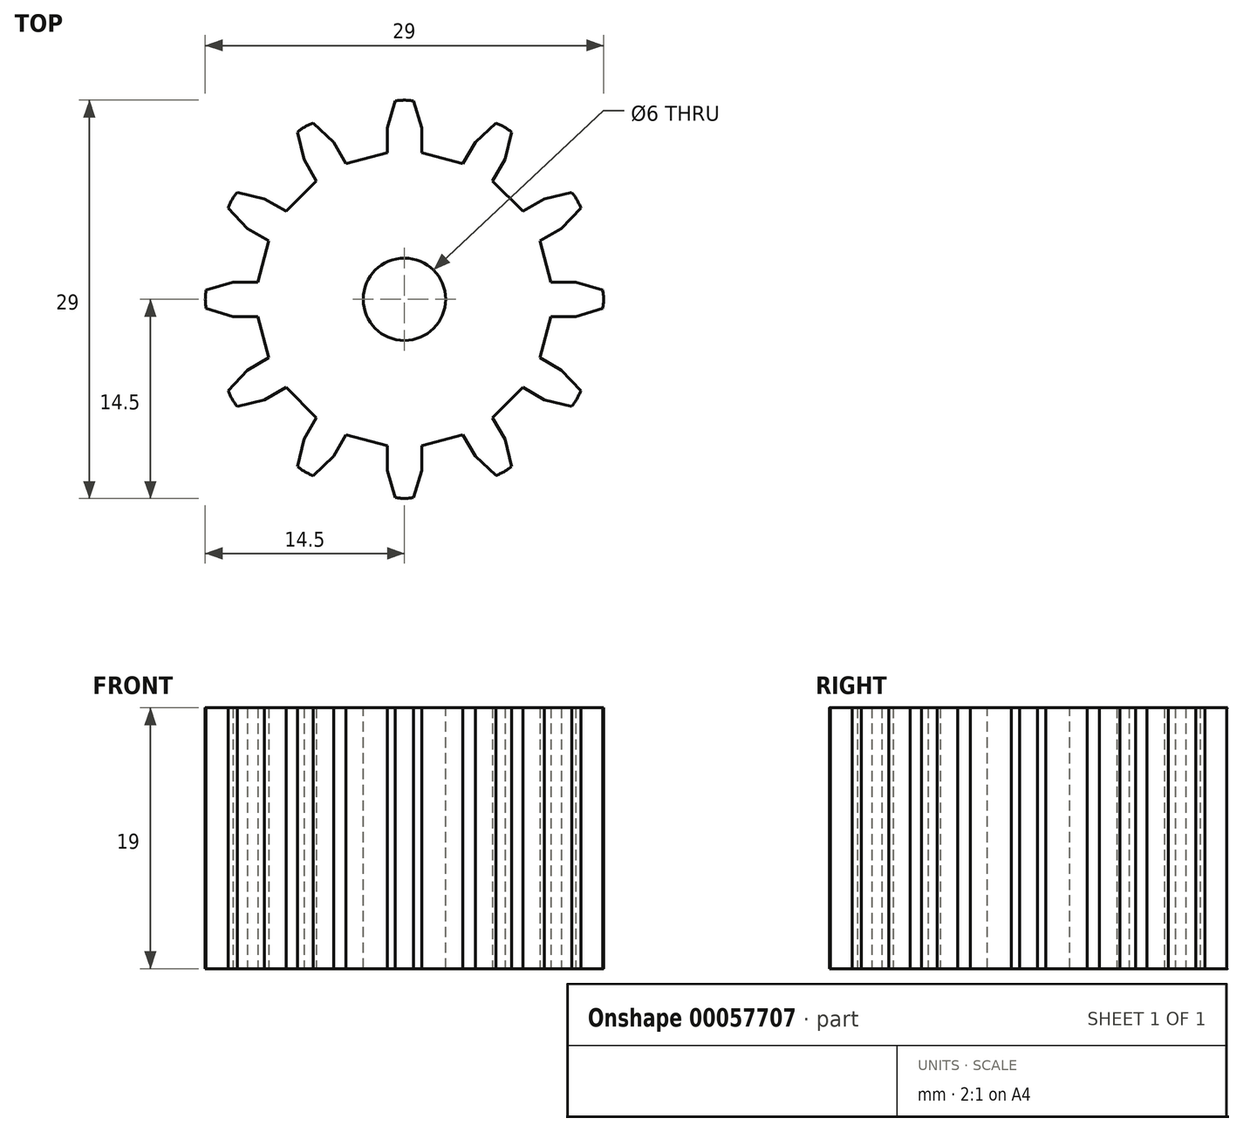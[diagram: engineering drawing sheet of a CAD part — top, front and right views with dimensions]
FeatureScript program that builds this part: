
annotation { "Feature Type Name" : "Feature", "Feature Type Description" : "" }
export const myFeature = defineFeature(function(context is Context, id is Id, definition is map)
    precondition{}
    {
        {
            var Q0;
            Q0=qCreatedBy(makeId("Top.planeOp"),FACE);
            var sketch = newSketch(context, id + "F0", { "sketchPlane" : qUnion([Q0])});
            skCircle(sketch, "E0", {"center": v(0, 0) * mm, "radius": 14.5 * mm});
            skArc(sketch, "E1", {"start": v(-1.25, 10.68) * mm, "mid": v(0, -10.75) * mm, "end": v(1.25, 10.68) * mm});
            skLineSegment(sketch, "E2", {"start": v(0, 10.75) * mm, "end": v(0, 14.5) * mm});
            skLineSegment(sketch, "E3.0", {"start": v(1.25, 10.68) * mm, "end": v(1.25, 14.29) * mm});
            skLineSegment(sketch, "E4.0", {"start": v(-1.25, 10.68) * mm, "end": v(-1.25, 14.29) * mm});
            skArc(sketch, "E5.trimOffspring", {"start": v(1.25, 14.29) * mm, "mid": v(0, 14.5) * mm, "end": v(-1.25, 14.29) * mm});
            skLineSegment(sketch, "E6", {"start": v(-1.25, 14.29) * mm, "end": v(-1.25, 14.45) * mm});
            skLineSegment(sketch, "E7.1.0", {"start": v(-4.26, 9.87) * mm, "end": v(-6.06, 13) * mm});
            skArc(sketch, "E7.1.1", {"start": v(-6.06, 13) * mm, "mid": v(-7.25, 12.56) * mm, "end": v(-8.23, 11.75) * mm});
            skLineSegment(sketch, "E7.1.2", {"start": v(-6.42, 8.62) * mm, "end": v(-8.23, 11.75) * mm});
            skLineSegment(sketch, "E7.2.0", {"start": v(-8.62, 6.42) * mm, "end": v(-11.75, 8.23) * mm});
            skArc(sketch, "E7.2.1", {"start": v(-11.75, 8.23) * mm, "mid": v(-12.56, 7.25) * mm, "end": v(-13, 6.06) * mm});
            skLineSegment(sketch, "E7.2.2", {"start": v(-9.87, 4.26) * mm, "end": v(-13, 6.06) * mm});
            skLineSegment(sketch, "E7.3.0", {"start": v(-10.68, 1.25) * mm, "end": v(-14.29, 1.25) * mm});
            skArc(sketch, "E7.3.1", {"start": v(-14.29, 1.25) * mm, "mid": v(-14.5, 0) * mm, "end": v(-14.29, -1.25) * mm});
            skLineSegment(sketch, "E7.3.2", {"start": v(-10.68, -1.25) * mm, "end": v(-14.29, -1.25) * mm});
            skLineSegment(sketch, "E7.4.0", {"start": v(-9.87, -4.26) * mm, "end": v(-13, -6.06) * mm});
            skArc(sketch, "E7.4.1", {"start": v(-13, -6.06) * mm, "mid": v(-12.56, -7.25) * mm, "end": v(-11.75, -8.23) * mm});
            skLineSegment(sketch, "E7.4.2", {"start": v(-8.62, -6.42) * mm, "end": v(-11.75, -8.23) * mm});
            skLineSegment(sketch, "E7.5.0", {"start": v(-6.42, -8.62) * mm, "end": v(-8.23, -11.75) * mm});
            skArc(sketch, "E7.5.1", {"start": v(-8.23, -11.75) * mm, "mid": v(-7.25, -12.56) * mm, "end": v(-6.06, -13) * mm});
            skLineSegment(sketch, "E7.5.2", {"start": v(-4.26, -9.87) * mm, "end": v(-6.06, -13) * mm});
            skLineSegment(sketch, "E7.6.0", {"start": v(-1.25, -10.68) * mm, "end": v(-1.25, -14.29) * mm});
            skArc(sketch, "E7.6.1", {"start": v(-1.25, -14.29) * mm, "mid": v(0, -14.5) * mm, "end": v(1.25, -14.29) * mm});
            skLineSegment(sketch, "E7.6.2", {"start": v(1.25, -10.68) * mm, "end": v(1.25, -14.29) * mm});
            skLineSegment(sketch, "E7.7.0", {"start": v(4.26, -9.87) * mm, "end": v(6.06, -13) * mm});
            skArc(sketch, "E7.7.1", {"start": v(6.06, -13) * mm, "mid": v(7.25, -12.56) * mm, "end": v(8.23, -11.75) * mm});
            skLineSegment(sketch, "E7.7.2", {"start": v(6.42, -8.62) * mm, "end": v(8.23, -11.75) * mm});
            skLineSegment(sketch, "E7.8.0", {"start": v(8.62, -6.42) * mm, "end": v(11.75, -8.23) * mm});
            skArc(sketch, "E7.8.1", {"start": v(11.75, -8.23) * mm, "mid": v(12.56, -7.25) * mm, "end": v(13, -6.06) * mm});
            skLineSegment(sketch, "E7.8.2", {"start": v(9.87, -4.26) * mm, "end": v(13, -6.06) * mm});
            skLineSegment(sketch, "E7.9.0", {"start": v(10.68, -1.25) * mm, "end": v(14.29, -1.25) * mm});
            skArc(sketch, "E7.9.1", {"start": v(14.29, -1.25) * mm, "mid": v(14.5, 0) * mm, "end": v(14.29, 1.25) * mm});
            skLineSegment(sketch, "E7.9.2", {"start": v(10.68, 1.25) * mm, "end": v(14.29, 1.25) * mm});
            skLineSegment(sketch, "E7.10.0", {"start": v(9.87, 4.26) * mm, "end": v(13, 6.06) * mm});
            skArc(sketch, "E7.10.1", {"start": v(13, 6.06) * mm, "mid": v(12.56, 7.25) * mm, "end": v(11.75, 8.23) * mm});
            skLineSegment(sketch, "E7.10.2", {"start": v(8.62, 6.42) * mm, "end": v(11.75, 8.23) * mm});
            skLineSegment(sketch, "E7.11.0", {"start": v(6.42, 8.62) * mm, "end": v(8.23, 11.75) * mm});
            skArc(sketch, "E7.11.1", {"start": v(8.23, 11.75) * mm, "mid": v(7.25, 12.56) * mm, "end": v(6.06, 13) * mm});
            skLineSegment(sketch, "E7.11.2", {"start": v(4.26, 9.87) * mm, "end": v(6.06, 13) * mm});
            skLineSegment(sketch, "E8", {"start": v(-1.25, 14.45) * mm, "end": v(-0.66, 14.45) * mm});
            skLineSegment(sketch, "E9", {"start": v(-0.66, 14.45) * mm, "end": v(-1.25, 12.48) * mm});
            skLineSegment(sketch, "E10.MirrorCS", {"start": v(0.66, 14.45) * mm, "end": v(1.25, 12.48) * mm});
            skLineSegment(sketch, "E11.1.0", {"start": v(-7.8, 12.18) * mm, "end": v(-7.32, 10.18) * mm});
            skLineSegment(sketch, "E11.1.1", {"start": v(-6.65, 12.84) * mm, "end": v(-5.16, 11.43) * mm});
            skLineSegment(sketch, "E11.2.0", {"start": v(-12.84, 6.65) * mm, "end": v(-11.43, 5.16) * mm});
            skLineSegment(sketch, "E11.2.1", {"start": v(-12.18, 7.8) * mm, "end": v(-10.18, 7.32) * mm});
            skLineSegment(sketch, "E11.3.0", {"start": v(-14.45, -0.66) * mm, "end": v(-12.48, -1.25) * mm});
            skLineSegment(sketch, "E11.3.1", {"start": v(-14.45, 0.66) * mm, "end": v(-12.48, 1.25) * mm});
            skLineSegment(sketch, "E11.4.0", {"start": v(-12.18, -7.8) * mm, "end": v(-10.18, -7.32) * mm});
            skLineSegment(sketch, "E11.4.1", {"start": v(-12.84, -6.65) * mm, "end": v(-11.43, -5.16) * mm});
            skLineSegment(sketch, "E11.5.0", {"start": v(-6.65, -12.84) * mm, "end": v(-5.16, -11.43) * mm});
            skLineSegment(sketch, "E11.5.1", {"start": v(-7.8, -12.18) * mm, "end": v(-7.32, -10.18) * mm});
            skLineSegment(sketch, "E11.6.0", {"start": v(0.66, -14.45) * mm, "end": v(1.25, -12.48) * mm});
            skLineSegment(sketch, "E11.6.1", {"start": v(-0.66, -14.45) * mm, "end": v(-1.25, -12.48) * mm});
            skLineSegment(sketch, "E11.7.0", {"start": v(7.8, -12.18) * mm, "end": v(7.32, -10.18) * mm});
            skLineSegment(sketch, "E11.7.1", {"start": v(6.65, -12.84) * mm, "end": v(5.16, -11.43) * mm});
            skLineSegment(sketch, "E11.8.0", {"start": v(12.84, -6.65) * mm, "end": v(11.43, -5.16) * mm});
            skLineSegment(sketch, "E11.8.1", {"start": v(12.18, -7.8) * mm, "end": v(10.18, -7.32) * mm});
            skLineSegment(sketch, "E11.9.0", {"start": v(14.45, 0.66) * mm, "end": v(12.48, 1.25) * mm});
            skLineSegment(sketch, "E11.9.1", {"start": v(14.45, -0.66) * mm, "end": v(12.48, -1.25) * mm});
            skLineSegment(sketch, "E11.10.0", {"start": v(12.18, 7.8) * mm, "end": v(10.18, 7.32) * mm});
            skLineSegment(sketch, "E11.10.1", {"start": v(12.84, 6.65) * mm, "end": v(11.43, 5.16) * mm});
            skLineSegment(sketch, "E11.11.0", {"start": v(6.65, 12.84) * mm, "end": v(5.16, 11.43) * mm});
            skLineSegment(sketch, "E11.11.1", {"start": v(7.8, 12.18) * mm, "end": v(7.32, 10.18) * mm});
            skSolve(sketch);
        }
        {
            var Q0;
            {var subQ0=sQuery(id+"F0.wireOp",EDGE,"E1");var subQ22=sQuery(id+"F0.wireOp",EDGE,"E4.0");var subQ23=makeQuery(id+"F0.imprint","INTERSECT",VERTEX,{"derivedFrom":[subQ0,subQ22]});Q0=makeQuery(id+"F0.imprint","IMPRINT",FACE,{"disambiguationData":[TD([[makeQuery(id+"F0.imprint","IMPRINT",EDGE,{"disambiguationData":[TD([[subQ23,-1.0]])],"derivedFrom":subQ0}),1.0]])]});}
            var Q1;
            {var subQ6=sQuery(id+"F0.wireOp",EDGE,"E7.1.0");var subQ7=sQuery(id+"F0.wireOp",EDGE,"E1");var subQ8=makeQuery(id+"F0.imprint","INTERSECT",VERTEX,{"derivedFrom":[subQ7,subQ6]});Q1=makeQuery(id+"F0.imprint","IMPRINT",FACE,{"disambiguationData":[TD([[makeQuery(id+"F0.imprint","IMPRINT",EDGE,{"disambiguationData":[TD([[subQ8,-1.0]])],"derivedFrom":subQ7}),-1.0]])]});}
            var Q2;
            {var subQ6=sQuery(id+"F0.wireOp",EDGE,"E7.2.0");var subQ7=sQuery(id+"F0.wireOp",EDGE,"E1");var subQ8=makeQuery(id+"F0.imprint","INTERSECT",VERTEX,{"derivedFrom":[subQ7,subQ6]});Q2=makeQuery(id+"F0.imprint","IMPRINT",FACE,{"disambiguationData":[TD([[makeQuery(id+"F0.imprint","IMPRINT",EDGE,{"disambiguationData":[TD([[subQ8,-1.0]])],"derivedFrom":subQ7}),-1.0]])]});}
            var Q3;
            {var subQ8=sQuery(id+"F0.wireOp",EDGE,"E7.3.0");var subQ9=sQuery(id+"F0.wireOp",EDGE,"E1");var subQ10=makeQuery(id+"F0.imprint","INTERSECT",VERTEX,{"derivedFrom":[subQ9,subQ8]});Q3=makeQuery(id+"F0.imprint","IMPRINT",FACE,{"disambiguationData":[TD([[makeQuery(id+"F0.imprint","IMPRINT",EDGE,{"disambiguationData":[TD([[subQ10,-1.0]])],"derivedFrom":subQ9}),-1.0]])]});}
            var Q4;
            {var subQ6=sQuery(id+"F0.wireOp",EDGE,"E7.11.0");var subQ7=sQuery(id+"F0.wireOp",EDGE,"E1");var subQ8=makeQuery(id+"F0.imprint","INTERSECT",VERTEX,{"derivedFrom":[subQ7,subQ6]});Q4=makeQuery(id+"F0.imprint","IMPRINT",FACE,{"disambiguationData":[TD([[makeQuery(id+"F0.imprint","IMPRINT",EDGE,{"disambiguationData":[TD([[subQ8,-1.0]])],"derivedFrom":subQ7}),-1.0]])]});}
            var Q5;
            {var subQ4=sQuery(id+"F0.wireOp",EDGE,"E7.10.0");var subQ5=sQuery(id+"F0.wireOp",EDGE,"E1");var subQ6=makeQuery(id+"F0.imprint","INTERSECT",VERTEX,{"derivedFrom":[subQ5,subQ4]});Q5=makeQuery(id+"F0.imprint","IMPRINT",FACE,{"disambiguationData":[TD([[makeQuery(id+"F0.imprint","IMPRINT",EDGE,{"disambiguationData":[TD([[subQ6,-1.0]])],"derivedFrom":subQ5}),-1.0]])]});}
            var Q6;
            {var subQ6=sQuery(id+"F0.wireOp",EDGE,"E7.9.0");var subQ7=sQuery(id+"F0.wireOp",EDGE,"E1");var subQ8=makeQuery(id+"F0.imprint","INTERSECT",VERTEX,{"derivedFrom":[subQ7,subQ6]});Q6=makeQuery(id+"F0.imprint","IMPRINT",FACE,{"disambiguationData":[TD([[makeQuery(id+"F0.imprint","IMPRINT",EDGE,{"disambiguationData":[TD([[subQ8,-1.0]])],"derivedFrom":subQ7}),-1.0]])]});}
            var Q7;
            {var subQ6=sQuery(id+"F0.wireOp",EDGE,"E7.6.0");var subQ7=sQuery(id+"F0.wireOp",EDGE,"E1");var subQ8=makeQuery(id+"F0.imprint","INTERSECT",VERTEX,{"derivedFrom":[subQ7,subQ6]});Q7=makeQuery(id+"F0.imprint","IMPRINT",FACE,{"disambiguationData":[TD([[makeQuery(id+"F0.imprint","IMPRINT",EDGE,{"disambiguationData":[TD([[subQ8,-1.0]])],"derivedFrom":subQ7}),-1.0]])]});}
            var Q8;
            {var subQ0=sQuery(id+"F0.wireOp",EDGE,"E7.5.0");var subQ1=sQuery(id+"F0.wireOp",EDGE,"E1");var subQ2=makeQuery(id+"F0.imprint","INTERSECT",VERTEX,{"derivedFrom":[subQ1,subQ0]});Q8=makeQuery(id+"F0.imprint","IMPRINT",FACE,{"disambiguationData":[TD([[makeQuery(id+"F0.imprint","IMPRINT",EDGE,{"disambiguationData":[TD([[subQ2,-1.0]])],"derivedFrom":subQ1}),-1.0]])]});}
            var Q9;
            {var subQ6=sQuery(id+"F0.wireOp",EDGE,"E7.4.0");var subQ7=sQuery(id+"F0.wireOp",EDGE,"E1");var subQ8=makeQuery(id+"F0.imprint","INTERSECT",VERTEX,{"derivedFrom":[subQ7,subQ6]});Q9=makeQuery(id+"F0.imprint","IMPRINT",FACE,{"disambiguationData":[TD([[makeQuery(id+"F0.imprint","IMPRINT",EDGE,{"disambiguationData":[TD([[subQ8,-1.0]])],"derivedFrom":subQ7}),-1.0]])]});}
            var Q10;
            {var subQ4=sQuery(id+"F0.wireOp",EDGE,"E7.8.0");var subQ5=sQuery(id+"F0.wireOp",EDGE,"E1");var subQ6=makeQuery(id+"F0.imprint","INTERSECT",VERTEX,{"derivedFrom":[subQ5,subQ4]});Q10=makeQuery(id+"F0.imprint","IMPRINT",FACE,{"disambiguationData":[TD([[makeQuery(id+"F0.imprint","IMPRINT",EDGE,{"disambiguationData":[TD([[subQ6,-1.0]])],"derivedFrom":subQ5}),-1.0]])]});}
            var Q11;
            {var subQ6=sQuery(id+"F0.wireOp",EDGE,"E7.7.0");var subQ7=sQuery(id+"F0.wireOp",EDGE,"E1");var subQ8=makeQuery(id+"F0.imprint","INTERSECT",VERTEX,{"derivedFrom":[subQ7,subQ6]});Q11=makeQuery(id+"F0.imprint","IMPRINT",FACE,{"disambiguationData":[TD([[makeQuery(id+"F0.imprint","IMPRINT",EDGE,{"disambiguationData":[TD([[subQ8,-1.0]])],"derivedFrom":subQ7}),-1.0]])]});}
            extrude(context, id + "F1", {"entities" : qUnion([Q0, Q1, Q2, Q3, Q4, Q5, Q6, Q7, Q8, Q9, Q10, Q11]), "depth" : 19 * mm});
        }
        {
            var Q0;
            Q0=makeQuery(id+"F1.opExtrude","CAP_FACE",FACE,{"disambiguationData":[OSD([sQuery(id+"F0.wireOp",EDGE,"E1"),sQuery(id+"F0.wireOp",EDGE,"E3.0"),sQuery(id+"F0.wireOp",EDGE,"E4.0"),sQuery(id+"F0.wireOp",EDGE,"E5.trimOffspring"),sQuery(id+"F0.wireOp",EDGE,"E7.1.0"),sQuery(id+"F0.wireOp",EDGE,"E7.1.1"),sQuery(id+"F0.wireOp",EDGE,"E7.1.2"),sQuery(id+"F0.wireOp",EDGE,"E7.2.0"),sQuery(id+"F0.wireOp",EDGE,"E7.2.1"),sQuery(id+"F0.wireOp",EDGE,"E7.2.2"),sQuery(id+"F0.wireOp",EDGE,"E7.3.0"),sQuery(id+"F0.wireOp",EDGE,"E7.3.1"),sQuery(id+"F0.wireOp",EDGE,"E7.3.2"),sQuery(id+"F0.wireOp",EDGE,"E7.4.0"),sQuery(id+"F0.wireOp",EDGE,"E7.4.1"),sQuery(id+"F0.wireOp",EDGE,"E7.4.2"),sQuery(id+"F0.wireOp",EDGE,"E7.5.0"),sQuery(id+"F0.wireOp",EDGE,"E7.5.1"),sQuery(id+"F0.wireOp",EDGE,"E7.5.2"),sQuery(id+"F0.wireOp",EDGE,"E7.6.0"),sQuery(id+"F0.wireOp",EDGE,"E7.6.1"),sQuery(id+"F0.wireOp",EDGE,"E7.6.2"),sQuery(id+"F0.wireOp",EDGE,"E7.7.0"),sQuery(id+"F0.wireOp",EDGE,"E7.7.1"),sQuery(id+"F0.wireOp",EDGE,"E7.7.2"),sQuery(id+"F0.wireOp",EDGE,"E7.8.0"),sQuery(id+"F0.wireOp",EDGE,"E7.8.1"),sQuery(id+"F0.wireOp",EDGE,"E7.8.2"),sQuery(id+"F0.wireOp",EDGE,"E7.9.0"),sQuery(id+"F0.wireOp",EDGE,"E7.9.1"),sQuery(id+"F0.wireOp",EDGE,"E7.9.2"),sQuery(id+"F0.wireOp",EDGE,"E7.10.0"),sQuery(id+"F0.wireOp",EDGE,"E7.10.1"),sQuery(id+"F0.wireOp",EDGE,"E7.10.2"),sQuery(id+"F0.wireOp",EDGE,"E7.11.0"),sQuery(id+"F0.wireOp",EDGE,"E7.11.1"),sQuery(id+"F0.wireOp",EDGE,"E7.11.2")])],"isStart":false});
            var sketch = newSketch(context, id + "F2", { "sketchPlane" : qUnion([Q0])});
            skCircle(sketch, "E12", {"center": v(0, 0) * mm, "radius": 3 * mm});
            skSolve(sketch);
        }
        {
            var Q0;
            Q0 = qSketchRegion(id + "F2", true);
            extrude(context, id + "F3", {"entities" : qUnion([Q0]), "operationType" : NewBodyOperationType.REMOVE, "endBound" : BoundingType.THROUGH_ALL, "oppositeDirection" : true, "depth" : 25 * mm});
        }
        {
            var Q0;
            Q0=makeQuery(id+"F1.opExtrude","CAP_FACE",FACE,{"disambiguationData":[OSD([sQuery(id+"F0.wireOp",EDGE,"E1"),sQuery(id+"F0.wireOp",EDGE,"E3.0"),sQuery(id+"F0.wireOp",EDGE,"E4.0"),sQuery(id+"F0.wireOp",EDGE,"E5.trimOffspring"),sQuery(id+"F0.wireOp",EDGE,"E7.1.0"),sQuery(id+"F0.wireOp",EDGE,"E7.1.1"),sQuery(id+"F0.wireOp",EDGE,"E7.1.2"),sQuery(id+"F0.wireOp",EDGE,"E7.2.0"),sQuery(id+"F0.wireOp",EDGE,"E7.2.1"),sQuery(id+"F0.wireOp",EDGE,"E7.2.2"),sQuery(id+"F0.wireOp",EDGE,"E7.3.0"),sQuery(id+"F0.wireOp",EDGE,"E7.3.1"),sQuery(id+"F0.wireOp",EDGE,"E7.3.2"),sQuery(id+"F0.wireOp",EDGE,"E7.4.0"),sQuery(id+"F0.wireOp",EDGE,"E7.4.1"),sQuery(id+"F0.wireOp",EDGE,"E7.4.2"),sQuery(id+"F0.wireOp",EDGE,"E7.5.0"),sQuery(id+"F0.wireOp",EDGE,"E7.5.1"),sQuery(id+"F0.wireOp",EDGE,"E7.5.2"),sQuery(id+"F0.wireOp",EDGE,"E7.6.0"),sQuery(id+"F0.wireOp",EDGE,"E7.6.1"),sQuery(id+"F0.wireOp",EDGE,"E7.6.2"),sQuery(id+"F0.wireOp",EDGE,"E7.7.0"),sQuery(id+"F0.wireOp",EDGE,"E7.7.1"),sQuery(id+"F0.wireOp",EDGE,"E7.7.2"),sQuery(id+"F0.wireOp",EDGE,"E7.8.0"),sQuery(id+"F0.wireOp",EDGE,"E7.8.1"),sQuery(id+"F0.wireOp",EDGE,"E7.8.2"),sQuery(id+"F0.wireOp",EDGE,"E7.9.0"),sQuery(id+"F0.wireOp",EDGE,"E7.9.1"),sQuery(id+"F0.wireOp",EDGE,"E7.9.2"),sQuery(id+"F0.wireOp",EDGE,"E7.10.0"),sQuery(id+"F0.wireOp",EDGE,"E7.10.1"),sQuery(id+"F0.wireOp",EDGE,"E7.10.2"),sQuery(id+"F0.wireOp",EDGE,"E7.11.0"),sQuery(id+"F0.wireOp",EDGE,"E7.11.1"),sQuery(id+"F0.wireOp",EDGE,"E7.11.2")])],"isStart":false});
            var sketch = newSketch(context, id + "F4", { "sketchPlane" : qUnion([Q0])});
            skLineSegment(sketch, "E13", {"start": v(1.25, 10.68) * mm, "end": v(4.26, 9.87) * mm});
            skLineSegment(sketch, "E14", {"start": v(4.26, 9.87) * mm, "end": v(6.42, 8.62) * mm});
            skLineSegment(sketch, "E15", {"start": v(6.42, 8.62) * mm, "end": v(8.62, 6.42) * mm});
            skLineSegment(sketch, "E16", {"start": v(8.62, 6.42) * mm, "end": v(9.87, 4.26) * mm});
            skLineSegment(sketch, "E17", {"start": v(9.87, 4.26) * mm, "end": v(10.68, 1.25) * mm});
            skLineSegment(sketch, "E18", {"start": v(10.68, 1.25) * mm, "end": v(10.68, -1.25) * mm});
            skLineSegment(sketch, "E19", {"start": v(10.68, -1.25) * mm, "end": v(9.87, -4.26) * mm});
            skLineSegment(sketch, "E20", {"start": v(9.87, -4.26) * mm, "end": v(8.62, -6.42) * mm});
            skLineSegment(sketch, "E21", {"start": v(8.62, -6.42) * mm, "end": v(6.42, -8.62) * mm});
            skLineSegment(sketch, "E22", {"start": v(6.42, -8.62) * mm, "end": v(4.26, -9.87) * mm});
            skLineSegment(sketch, "E23", {"start": v(4.26, -9.87) * mm, "end": v(1.25, -10.68) * mm});
            skLineSegment(sketch, "E24", {"start": v(1.25, -10.68) * mm, "end": v(-1.25, -10.68) * mm});
            skLineSegment(sketch, "E25", {"start": v(-1.25, -10.68) * mm, "end": v(-4.26, -9.87) * mm});
            skLineSegment(sketch, "E26", {"start": v(-4.26, -9.87) * mm, "end": v(-6.42, -8.62) * mm});
            skLineSegment(sketch, "E27", {"start": v(-6.42, -8.62) * mm, "end": v(-8.62, -6.42) * mm});
            skLineSegment(sketch, "E28", {"start": v(-8.62, -6.42) * mm, "end": v(-9.87, -4.26) * mm});
            skLineSegment(sketch, "E29", {"start": v(-9.87, -4.26) * mm, "end": v(-10.68, -1.25) * mm});
            skLineSegment(sketch, "E30", {"start": v(-10.68, -1.25) * mm, "end": v(-10.68, 1.25) * mm});
            skLineSegment(sketch, "E31", {"start": v(-10.68, 1.25) * mm, "end": v(-9.87, 4.26) * mm});
            skLineSegment(sketch, "E32", {"start": v(-9.87, 4.26) * mm, "end": v(-8.62, 6.42) * mm});
            skLineSegment(sketch, "E33", {"start": v(-8.62, 6.42) * mm, "end": v(-6.42, 8.62) * mm});
            skLineSegment(sketch, "E34", {"start": v(-6.42, 8.62) * mm, "end": v(-4.26, 9.87) * mm});
            skLineSegment(sketch, "E35", {"start": v(-4.26, 9.87) * mm, "end": v(-1.25, 10.68) * mm});
            skLineSegment(sketch, "E36", {"start": v(-1.25, 10.68) * mm, "end": v(1.25, 10.68) * mm});
            skSolve(sketch);
        }
        {
            var Q0;
            Q0=makeQuery(id+"F4.imprint","IMPRINT",FACE,{"disambiguationData":[TD([[makeQuery(id+"F4.imprint","IMPRINT",EDGE,{"derivedFrom":sQuery(id+"F4.wireOp",EDGE,"E31")}),1.0]])]});
            var Q1;
            Q1=makeQuery(id+"F4.imprint","IMPRINT",FACE,{"disambiguationData":[TD([[makeQuery(id+"F4.imprint","IMPRINT",EDGE,{"derivedFrom":sQuery(id+"F4.wireOp",EDGE,"E29")}),1.0]])]});
            var Q2;
            Q2=makeQuery(id+"F4.imprint","IMPRINT",FACE,{"disambiguationData":[TD([[makeQuery(id+"F4.imprint","IMPRINT",EDGE,{"derivedFrom":sQuery(id+"F4.wireOp",EDGE,"E33")}),1.0]])]});
            var Q3;
            Q3=makeQuery(id+"F4.imprint","IMPRINT",FACE,{"disambiguationData":[TD([[makeQuery(id+"F4.imprint","IMPRINT",EDGE,{"derivedFrom":sQuery(id+"F4.wireOp",EDGE,"E35")}),1.0]])]});
            var Q4;
            Q4=makeQuery(id+"F4.imprint","IMPRINT",FACE,{"disambiguationData":[TD([[makeQuery(id+"F4.imprint","IMPRINT",EDGE,{"derivedFrom":sQuery(id+"F4.wireOp",EDGE,"E13")}),1.0]])]});
            var Q5;
            Q5=makeQuery(id+"F4.imprint","IMPRINT",FACE,{"disambiguationData":[TD([[makeQuery(id+"F4.imprint","IMPRINT",EDGE,{"derivedFrom":sQuery(id+"F4.wireOp",EDGE,"E15")}),1.0]])]});
            var Q6;
            Q6=makeQuery(id+"F4.imprint","IMPRINT",FACE,{"disambiguationData":[TD([[makeQuery(id+"F4.imprint","IMPRINT",EDGE,{"derivedFrom":sQuery(id+"F4.wireOp",EDGE,"E17")}),1.0]])]});
            var Q7;
            Q7=makeQuery(id+"F4.imprint","IMPRINT",FACE,{"disambiguationData":[TD([[makeQuery(id+"F4.imprint","IMPRINT",EDGE,{"derivedFrom":sQuery(id+"F4.wireOp",EDGE,"E19")}),1.0]])]});
            var Q8;
            Q8=makeQuery(id+"F4.imprint","IMPRINT",FACE,{"disambiguationData":[TD([[makeQuery(id+"F4.imprint","IMPRINT",EDGE,{"derivedFrom":sQuery(id+"F4.wireOp",EDGE,"E21")}),1.0]])]});
            var Q9;
            Q9=makeQuery(id+"F4.imprint","IMPRINT",FACE,{"disambiguationData":[TD([[makeQuery(id+"F4.imprint","IMPRINT",EDGE,{"derivedFrom":sQuery(id+"F4.wireOp",EDGE,"E23")}),1.0]])]});
            var Q10;
            Q10=makeQuery(id+"F4.imprint","IMPRINT",FACE,{"disambiguationData":[TD([[makeQuery(id+"F4.imprint","IMPRINT",EDGE,{"derivedFrom":sQuery(id+"F4.wireOp",EDGE,"E25")}),1.0]])]});
            var Q11;
            Q11=makeQuery(id+"F4.imprint","IMPRINT",FACE,{"disambiguationData":[TD([[makeQuery(id+"F4.imprint","IMPRINT",EDGE,{"derivedFrom":sQuery(id+"F4.wireOp",EDGE,"E27")}),1.0]])]});
            extrude(context, id + "F5", {"entities" : qUnion([Q0, Q1, Q2, Q3, Q4, Q5, Q6, Q7, Q8, Q9, Q10, Q11]), "operationType" : NewBodyOperationType.REMOVE, "endBound" : BoundingType.THROUGH_ALL, "oppositeDirection" : true, "depth" : 25 * mm});
        }
    });
